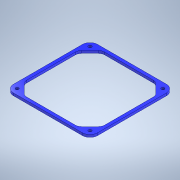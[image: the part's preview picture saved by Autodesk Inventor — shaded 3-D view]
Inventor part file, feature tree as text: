
AUTODESK INVENTOR PART (.ipt)
format: ipt  version: 2020.5 (Build 245400000, 400)  size: 139,264 bytes
history: native  units: mm
features: extrude x1, sketch x1
ambient origin geometry x8: Origin, YZ Plane, XZ Plane, XY Plane, X Axis, Y Axis, Z Axis, Center Point
bodies: Solid1 (feature_tree)
feature tree (2):
  extrude  "Extrusion1"  Depth=3.2mm TaperAngle=0.0deg
  sketch  "Sketch1"  dims[d23=40.0mm d25=360.0deg d28=3.2mm d29=0.0mm]
